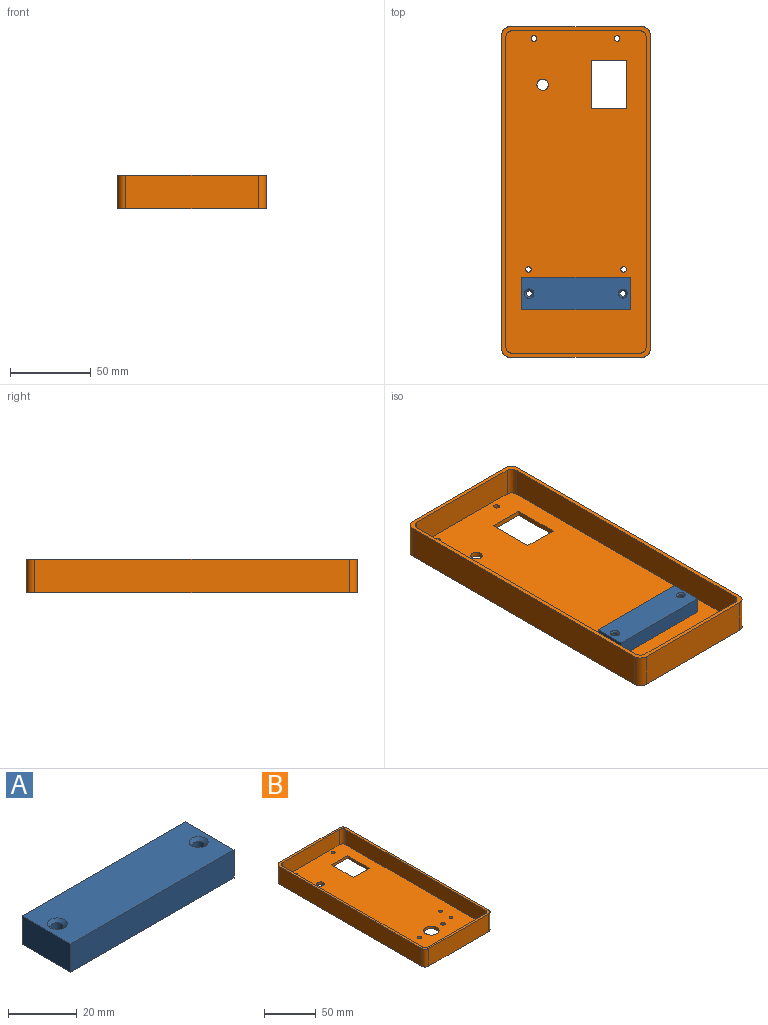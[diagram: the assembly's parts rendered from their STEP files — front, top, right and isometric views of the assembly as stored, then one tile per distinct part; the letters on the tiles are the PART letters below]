
ASSEMBLY  parts=2 mates=1
PART A: 10 faces, bbox 67x20x10 mm
  f0: plane 67x10mm, normal (0,1,0), area 670mm2, adj f1,f4,f6,f7
  f1: plane 20x10mm, normal (-1,0,0), area 200mm2, adj f0,f2,f6,f7
  f2: plane 67x10mm, normal (0,-1,0), area 670mm2, adj f1,f4,f6,f7
  f3: cylinder r=1.9mm len=9mm, axis (0,0,1), area 107.4mm2, adj f7,f9
  f4: plane 20x10mm, normal (1,0,0), area 200mm2, adj f0,f2,f6,f7
  f5: cylinder r=1.75mm len=9mm, axis (0,0,1), area 99mm2, adj f7,f8
  f6: plane 67x20mm, normal (0,0,1), area 1289.8mm2, adj f0,f1,f2,f4,f8,f9
  f7: plane 67x20mm, normal (0,0,-1), area 1319mm2, adj f0,f1,f2,f3,f4,f5
  f8: cone r=1.75mm half-angle=45deg, axis (0,0,1), area 20mm2, adj f5,f6
  f9: cone r=1.9mm half-angle=45deg, axis (0,0,1), area 21.3mm2, adj f3,f6
PART B: 33 faces, bbox 92x205x21 mm
  f0: plane 200x87mm, normal (0,0,1), area 16428.2mm2, adj f10,f11,f12,f13,f14,f15,f16,f17
  f1: plane 195x21mm, normal (-1,0,0), area 4095mm2, adj f2,f8,f9,f18
  f2: cylinder r=5mm len=21mm, axis (0,0,1), area 164.9mm2, adj f1,f3,f9,f18
  f3: plane 82x21mm, normal (0,-1,0), area 1722mm2, adj f2,f4,f9,f18
  f4: cylinder r=5mm len=21mm, axis (0,0,1), area 164.9mm2, adj f3,f5,f9,f18
  f5: plane 195x21mm, normal (1,0,0), area 4095mm2, adj f4,f6,f9,f18
  f6: cylinder r=5mm len=21mm, axis (0,0,1), area 164.9mm2, adj f5,f7,f9,f18
  f7: plane 82x21mm, normal (0,1,0), area 1722mm2, adj f6,f8,f9,f18
  f8: cylinder r=5mm len=21mm, axis (0,0,1), area 164.9mm2, adj f1,f7,f9,f18
  f9: plane 205x92mm, normal (0,0,-1), area 17880.5mm2, adj f1,f2,f3,f4,f5,f6,f7,f8
  f10: cylinder r=4mm len=18mm, axis (0,0,1), area 113.1mm2, adj f0,f11,f17,f18
  f11: plane 192x18mm, normal (1,0,0), area 3456mm2, adj f0,f10,f12,f18
  f12: cylinder r=4mm len=18mm, axis (0,0,1), area 113.1mm2, adj f0,f11,f13,f18
  f13: plane 79x18mm, normal (0,-1,0), area 1422mm2, adj f0,f12,f14,f18
  f14: cylinder r=4mm len=18mm, axis (0,0,1), area 113.1mm2, adj f0,f13,f15,f18
  f15: plane 192x18mm, normal (-1,0,0), area 3456mm2, adj f0,f14,f16,f18
  f16: cylinder r=4mm len=18mm, axis (0,0,1), area 113.1mm2, adj f0,f15,f17,f18
  f17: plane 79x18mm, normal (0,1,0), area 1422mm2, adj f0,f10,f16,f18
  f18: plane 205x92mm, normal (0,0,1), area 1452.3mm2, adj f1,f2,f3,f4,f5,f6,f7,f8
  f19: cylinder r=1.75mm len=3.5mm, axis (0,0,1), area 33mm2, adj f0,f9
  f20: cylinder r=1.75mm len=3.5mm, axis (0,0,1), area 33mm2, adj f0,f9
  f21: cylinder r=1.75mm len=3.5mm, axis (0,0,1), area 33mm2, adj f0,f9
  f22: plane 22x3mm, normal (0,-1,0), area 66mm2, adj f0,f9,f23,f25
  f23: plane 30x3mm, normal (1,0,0), area 90mm2, adj f0,f9,f22,f24
  f24: plane 22x3mm, normal (0,1,0), area 66mm2, adj f0,f9,f23,f25
  f25: plane 30x3mm, normal (-1,0,0), area 90mm2, adj f0,f9,f22,f24
  f26: cylinder r=3.5mm len=7mm, axis (0,0,1), area 66mm2, adj f0,f9
  f27: cylinder r=2mm len=4mm, axis (0,0,1), area 37.7mm2, adj f0,f9
  f28: cylinder r=7.5mm len=15mm, axis (0,0,1), area 141.4mm2, adj f0,f9
  f29: cylinder r=1.75mm len=3.5mm, axis (0,0,1), area 33mm2, adj f0,f9
  f30: cylinder r=1.75mm len=3.5mm, axis (0,0,1), area 33mm2, adj f0,f9
  f31: cylinder r=1.75mm len=3.5mm, axis (0,0,1), area 33mm2, adj f0,f9
  f32: cylinder r=2mm len=4mm, axis (0,0,1), area 37.7mm2, adj f0,f9
PLACE A t=(-12.29,-56.72,19.27)mm
PLACE B t=(-12.29,6.28,16.27)mm
MATE fastened A.f3 <-> B.f29  axis (0,0,-1) through (-41.29,-56.72,19.27)mm
